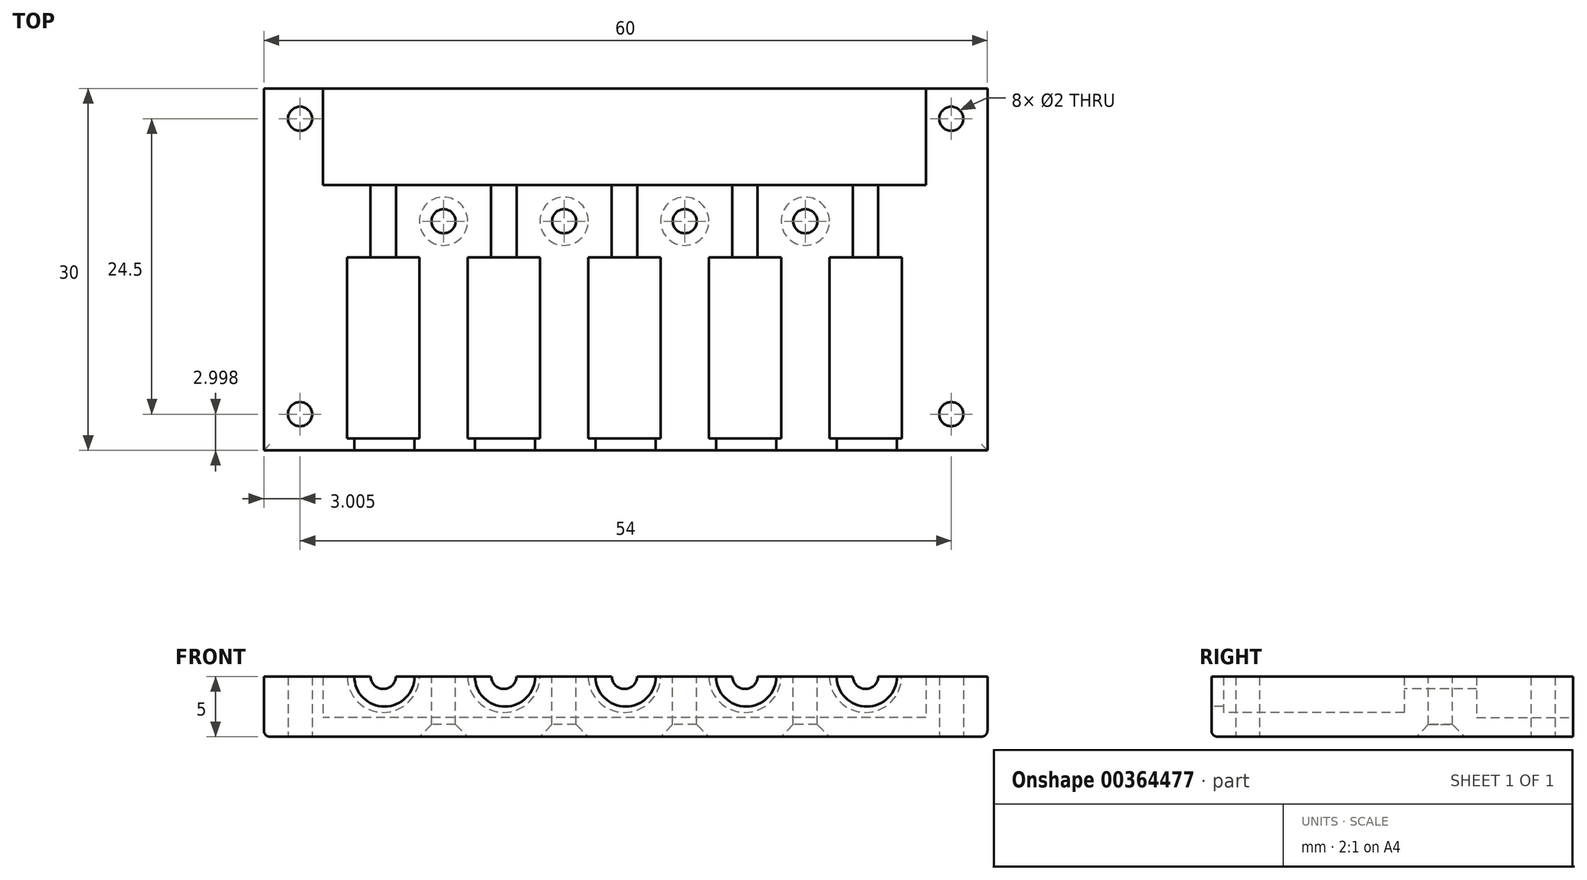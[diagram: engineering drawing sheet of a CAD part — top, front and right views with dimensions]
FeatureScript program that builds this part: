
annotation { "Feature Type Name" : "Feature", "Feature Type Description" : "" }
export const myFeature = defineFeature(function(context is Context, id is Id, definition is map)
    precondition{}
    {
        {
            var Q0;
            Q0=qCreatedBy(makeId("Top.planeOp"),FACE);
            var sketch = newSketch(context, id + "F0", { "sketchPlane" : qUnion([Q0])});
            skLineSegment(sketch, "E0.bottom", {"start": v(-32.95, 5.2) * mm, "end": v(27.05, 5.2) * mm});
            skLineSegment(sketch, "E0.top", {"start": v(-32.95, -19.8) * mm, "end": v(27.05, -19.8) * mm});
            skLineSegment(sketch, "E0.left", {"start": v(-32.95, 5.2) * mm, "end": v(-32.95, -19.8) * mm});
            skLineSegment(sketch, "E0.right", {"start": v(27.05, 5.2) * mm, "end": v(27.05, -19.8) * mm});
            skSolve(sketch);
        }
        {
            var Q0;
            Q0 = qSketchRegion(id + "F0", true);
            extrude(context, id + "F1", {"entities" : qUnion([Q0]), "depth" : 5 * mm});
        }
        {
            var Q0;
            Q0=makeQuery(id+"F1.opExtrude","SWEPT_FACE",FACE,{"disambiguationData":[OSD([sQuery(id+"F0.wireOp",EDGE,"E0.top")])]});
            var sketch = newSketch(context, id + "F2", { "sketchPlane" : qUnion([Q0])});
            skCircle(sketch, "E1", {"center": v(-22.95, 5) * mm, "radius": 2.5 * mm});
            skCircle(sketch, "E2.1.0.0", {"center": v(-12.95, 5) * mm, "radius": 2.5 * mm});
            skCircle(sketch, "E2.2.0.0", {"center": v(-2.95, 5) * mm, "radius": 2.5 * mm});
            skCircle(sketch, "E2.3.0.0", {"center": v(7.05, 5) * mm, "radius": 2.5 * mm});
            skCircle(sketch, "E2.4.0.0", {"center": v(17.05, 5) * mm, "radius": 2.5 * mm});
            skLineSegment(sketch, "E2.direction1", {"start": v(-22.95, 5) * mm, "end": v(-12.95, 5) * mm, "construction": true});
            skSolve(sketch);
        }
        {
            var Q0;
            Q0 = qSketchRegion(id + "F2", true);
            extrude(context, id + "F3", {"entities" : qUnion([Q0]), "operationType" : NewBodyOperationType.REMOVE, "oppositeDirection" : true, "depth" : 10 * mm});
        }
        {
            var Q0;
            Q0=makeQuery(id+"F1.opExtrude","SWEPT_FACE",FACE,{"disambiguationData":[OSD([sQuery(id+"F0.wireOp",EDGE,"E0.top")])]});
            cPlane(context, id + "F4", {"entities" : qUnion([Q0]), "cplaneType" : CPlaneType.OFFSET, "offset" : 1 * mm, "oppositeDirection" : true, "width" : 150 * mm, "height" : 150 * mm});
        }
        {
            var Q0;
            Q0=qCreatedBy(id+"F4.planeOp",FACE);
            var sketch = newSketch(context, id + "F5", { "sketchPlane" : qUnion([Q0])});
            skCircle(sketch, "E3", {"center": v(-23.05, 5.01) * mm, "radius": 3 * mm});
            skCircle(sketch, "E4.1.0.0", {"center": v(-13.05, 5.01) * mm, "radius": 3 * mm});
            skCircle(sketch, "E4.2.0.0", {"center": v(-3.05, 5.01) * mm, "radius": 3 * mm});
            skCircle(sketch, "E4.3.0.0", {"center": v(6.95, 5.01) * mm, "radius": 3 * mm});
            skCircle(sketch, "E4.4.0.0", {"center": v(16.95, 5.01) * mm, "radius": 3 * mm});
            skLineSegment(sketch, "E4.direction1", {"start": v(-23.05, 5.01) * mm, "end": v(-13.05, 5.01) * mm, "construction": true});
            skSolve(sketch);
        }
        {
            var Q0;
            Q0 = qSketchRegion(id + "F5", true);
            extrude(context, id + "F6", {"entities" : qUnion([Q0]), "operationType" : NewBodyOperationType.REMOVE, "oppositeDirection" : true, "depth" : 15 * mm});
        }
        {
            var Q0;
            Q0=makeQuery(id+"F6.boolean.opBoolean","COPY",FACE,{"derivedFrom":makeQuery(id+"F6.opExtrude","CAP_FACE",FACE,{"disambiguationData":[OSD([sQuery(id+"F5.wireOp",EDGE,"E3")])],"isStart":false})});
            var sketch = newSketch(context, id + "F7", { "sketchPlane" : qUnion([Q0])});
            skCircle(sketch, "E5", {"center": v(-23.05, 5.01) * mm, "radius": 1.05 * mm});
            skCircle(sketch, "E6.1.0.0", {"center": v(-13.05, 5.01) * mm, "radius": 1.05 * mm});
            skCircle(sketch, "E6.2.0.0", {"center": v(-3.05, 5.01) * mm, "radius": 1.05 * mm});
            skCircle(sketch, "E6.3.0.0", {"center": v(6.95, 5.01) * mm, "radius": 1.05 * mm});
            skCircle(sketch, "E6.4.0.0", {"center": v(16.95, 5.01) * mm, "radius": 1.05 * mm});
            skLineSegment(sketch, "E6.direction1", {"start": v(-23.05, 5.01) * mm, "end": v(-13.05, 5.01) * mm, "construction": true});
            skSolve(sketch);
        }
        {
            var Q0;
            Q0 = qSketchRegion(id + "F7", true);
            extrude(context, id + "F8", {"entities" : qUnion([Q0]), "operationType" : NewBodyOperationType.REMOVE, "oppositeDirection" : true, "depth" : 29 * mm});
        }
        {
            var Q0;
            Q0=makeQuery(id+"F1.opExtrude","SWEPT_FACE",FACE,{"disambiguationData":[OSD([sQuery(id+"F0.wireOp",EDGE,"E0.bottom")])]});
            var sketch = newSketch(context, id + "F9", { "sketchPlane" : qUnion([Q0])});
            skLineSegment(sketch, "E7.bottom", {"start": v(-21.95, 5) * mm, "end": v(28.05, 5) * mm});
            skLineSegment(sketch, "E7.top", {"start": v(-21.95, 1.58) * mm, "end": v(28.05, 1.58) * mm});
            skLineSegment(sketch, "E7.left", {"start": v(-21.95, 5) * mm, "end": v(-21.95, 1.58) * mm});
            skLineSegment(sketch, "E7.right", {"start": v(28.05, 5) * mm, "end": v(28.05, 1.58) * mm});
            skSolve(sketch);
        }
        {
            var Q0;
            Q0 = qSketchRegion(id + "F9", true);
            extrude(context, id + "F10", {"entities" : qUnion([Q0]), "operationType" : NewBodyOperationType.REMOVE, "oppositeDirection" : true, "depth" : 3 * mm});
        }
        {
            var Q0;
            Q0=makeQuery(id+"F1.opExtrude","SWEPT_FACE",FACE,{"disambiguationData":[OSD([sQuery(id+"F0.wireOp",EDGE,"E0.bottom")])]});
            extrude(context, id + "F11", {"entities" : qUnion([Q0]), "operationType" : NewBodyOperationType.ADD, "depth" : 5 * mm});
        }
        {
            var Q0;
            {var subQ0=sQuery(id+"F0.wireOp",EDGE,"E0.right");var subQ1=sQuery(id+"F0.wireOp",EDGE,"E0.bottom");Q0=makeQuery(id+"F11.boolean.opBoolean","MERGE",EDGE,{"derivedFrom":[makeQuery(id+"F1.opExtrude","CAP_EDGE",EDGE,{"disambiguationData":[OSD([subQ0])],"isStart":true}),makeQuery(id+"F11.opExtrude","SWEPT_EDGE",EDGE,{"disambiguationData":[OSD([subQ1,subQ0]),TDD([makeQuery(id+"F1.opExtrude","CAP_VERTEX",VERTEX,{"disambiguationData":[OSD([subQ1,subQ0])],"isStart":true})])]})]});}
            var Q1;
            Q1=makeQuery(id+"F1.opExtrude","CAP_EDGE",EDGE,{"disambiguationData":[OSD([sQuery(id+"F0.wireOp",EDGE,"E0.top")])],"isStart":true});
            var Q2;
            Q2=makeQuery(id+"FEIolAkUxVgGt6m_1.opLoft","SWEPT_EDGE",EDGE,{"disambiguationData":[OSD([sQuery(id+"F0.wireOp",EDGE,"E0.bottom"),sQuery(id+"F0.wireOp",EDGE,"E0.right"),sQuery(id+"F4cxA0SiljIs9s8_1.wireOp",EDGE,"Jk4UEFDV-4BQ6-7r7a-iLyf-OHepFeUpgrdx.top"),sQuery(id+"F4cxA0SiljIs9s8_1.wireOp",EDGE,"Jk4UEFDV-4BQ6-7r7a-iLyf-OHepFeUpgrdx.left")])]});
            var Q3;
            Q3=makeQuery(id+"FEIolAkUxVgGt6m_1.opLoft","MID_CAP_EDGE",EDGE,{"disambiguationData":[OSD([sQuery(id+"F4cxA0SiljIs9s8_1.wireOp",EDGE,"Jk4UEFDV-4BQ6-7r7a-iLyf-OHepFeUpgrdx.top"),sQuery(id+"F4cxA0SiljIs9s8_1.wireOp",EDGE,"Jk4UEFDV-4BQ6-7r7a-iLyf-OHepFeUpgrdx.left"),sQuery(id+"F4cxA0SiljIs9s8_1.wireOp",EDGE,"Jk4UEFDV-4BQ6-7r7a-iLyf-OHepFeUpgrdx.right")])],"capPos":1.0});
            var Q4;
            Q4=makeQuery(id+"FEIolAkUxVgGt6m_1.opLoft","SWEPT_EDGE",EDGE,{"disambiguationData":[OSD([sQuery(id+"F0.wireOp",EDGE,"E0.bottom"),sQuery(id+"F0.wireOp",EDGE,"E0.left"),sQuery(id+"F4cxA0SiljIs9s8_1.wireOp",EDGE,"Jk4UEFDV-4BQ6-7r7a-iLyf-OHepFeUpgrdx.top"),sQuery(id+"F4cxA0SiljIs9s8_1.wireOp",EDGE,"Jk4UEFDV-4BQ6-7r7a-iLyf-OHepFeUpgrdx.right")])]});
            var Q5;
            {var subQ0=sQuery(id+"F0.wireOp",EDGE,"E0.left");var subQ1=sQuery(id+"F0.wireOp",EDGE,"E0.bottom");Q5=makeQuery(id+"F11.boolean.opBoolean","MERGE",EDGE,{"derivedFrom":[makeQuery(id+"F1.opExtrude","CAP_EDGE",EDGE,{"disambiguationData":[OSD([subQ0])],"isStart":true}),makeQuery(id+"F11.opExtrude","SWEPT_EDGE",EDGE,{"disambiguationData":[OSD([subQ1,subQ0]),TDD([makeQuery(id+"F1.opExtrude","CAP_VERTEX",VERTEX,{"disambiguationData":[OSD([subQ1,subQ0])],"isStart":true})])]})]});}
            fillet(context, id + "F12", {"entities" : qUnion([Q0, Q1, Q2, Q3, Q4, Q5]), "radius" : 0.5 * mm, "tangentPropagation" : true, "allowEdgeOverflow" : false});
        }
        {
            var Q0;
            {var subQ0=sQuery(id+"F0.wireOp",EDGE,"E0.bottom");Q0=makeQuery(id+"F11.boolean.opBoolean","MERGE",FACE,{"derivedFrom":[makeQuery(id+"F1.opExtrude","CAP_FACE",FACE,{"disambiguationData":[OSD([subQ0,sQuery(id+"F0.wireOp",EDGE,"E0.top"),sQuery(id+"F0.wireOp",EDGE,"E0.left"),sQuery(id+"F0.wireOp",EDGE,"E0.right")])],"isStart":true}),makeQuery(id+"F11.opExtrude","SWEPT_FACE",FACE,{"disambiguationData":[OSD([subQ0]),TDD([makeQuery(id+"F1.opExtrude","CAP_EDGE",EDGE,{"disambiguationData":[OSD([subQ0])],"isStart":true})])]})]});}
            var sketch = newSketch(context, id + "F13", { "sketchPlane" : qUnion([Q0])});
            skLineSegment(sketch, "E8", {"start": v(-2.95, 19.3) * mm, "end": v(-2.95, -10.2) * mm});
            skCircle(sketch, "E9", {"center": v(-29.95, 16.8) * mm, "radius": 1 * mm});
            skCircle(sketch, "E10.MirrorC", {"center": v(24.05, 16.8) * mm, "radius": 1 * mm});
            skSolve(sketch);
        }
        {
            var Q0;
            {var subQ7=sQuery(id+"F13.wireOp",EDGE,"E8");Q0=makeQuery(id+"F13.imprint","IMPRINT",FACE,{"disambiguationData":[TD([[makeQuery(id+"F13.imprint","IMPRINT",EDGE,{"derivedFrom":subQ7}),-1.0]])]});}
            var sketch = newSketch(context, id + "F14", { "sketchPlane" : qUnion([Q0])});
            skCircle(sketch, "E11", {"center": v(-29.95, -7.7) * mm, "radius": 1 * mm});
            skCircle(sketch, "E12.MirrorC", {"center": v(24.05, -7.7) * mm, "radius": 1 * mm});
            skSolve(sketch);
        }
        {
            var Q0;
            Q0 = qSketchRegion(id + "F14", true);
            var Q1;
            Q1 = qSketchRegion(id + "F13", true);
            extrude(context, id + "F15", {"entities" : qUnion([Q0, Q1]), "operationType" : NewBodyOperationType.REMOVE, "endBound" : BoundingType.THROUGH_ALL, "oppositeDirection" : true, "depth" : 25 * mm});
        }
        {
            var Q0;
            {var subQ0=sQuery(id+"F5.wireOp",EDGE,"E4.4.0.0");var subQ1=sQuery(id+"F0.wireOp",EDGE,"E0.top");var subQ2=sQuery(id+"F5.wireOp",EDGE,"E4.3.0.0");var subQ3=sQuery(id+"F0.wireOp",EDGE,"E0.bottom");Q0=makeQuery(id+"F8.boolean.opBoolean","SPLIT",FACE,{"disambiguationData":[TD([makeQuery(id+"F1.opExtrude","SWEPT_FACE",FACE,{"disambiguationData":[OSD([subQ3])]}),makeQuery(id+"F1.opExtrude","SWEPT_FACE",FACE,{"disambiguationData":[OSD([subQ1])]}),makeQuery(id+"F3.boolean.opBoolean","COPY",FACE,{"derivedFrom":makeQuery(id+"F3.opExtrude","SWEPT_FACE",FACE,{"disambiguationData":[OSD([sQuery(id+"F2.wireOp",EDGE,"E2.3.0.0")])]})}),makeQuery(id+"F3.boolean.opBoolean","COPY",FACE,{"derivedFrom":makeQuery(id+"F3.opExtrude","SWEPT_FACE",FACE,{"disambiguationData":[OSD([sQuery(id+"F2.wireOp",EDGE,"E2.4.0.0")])]})}),makeQuery(id+"F6.boolean.opBoolean","COPY",FACE,{"derivedFrom":makeQuery(id+"F6.opExtrude","SWEPT_FACE",FACE,{"disambiguationData":[OSD([subQ2])]})}),makeQuery(id+"F6.boolean.opBoolean","COPY",FACE,{"derivedFrom":makeQuery(id+"F6.opExtrude","CAP_FACE",FACE,{"disambiguationData":[OSD([subQ2])],"isStart":true})}),makeQuery(id+"F6.boolean.opBoolean","COPY",FACE,{"derivedFrom":makeQuery(id+"F6.opExtrude","CAP_FACE",FACE,{"disambiguationData":[OSD([subQ2])],"isStart":false})}),makeQuery(id+"F6.boolean.opBoolean","COPY",FACE,{"derivedFrom":makeQuery(id+"F6.opExtrude","SWEPT_FACE",FACE,{"disambiguationData":[OSD([subQ0])]})}),makeQuery(id+"F6.boolean.opBoolean","COPY",FACE,{"derivedFrom":makeQuery(id+"F6.opExtrude","CAP_FACE",FACE,{"disambiguationData":[OSD([subQ0])],"isStart":true})}),makeQuery(id+"F6.boolean.opBoolean","COPY",FACE,{"derivedFrom":makeQuery(id+"F6.opExtrude","CAP_FACE",FACE,{"disambiguationData":[OSD([subQ0])],"isStart":false})}),makeQuery(id+"F8.opExtrude","SWEPT_FACE",FACE,{"disambiguationData":[OSD([sQuery(id+"F7.wireOp",EDGE,"E6.3.0.0")])]}),makeQuery(id+"F8.opExtrude","SWEPT_FACE",FACE,{"disambiguationData":[OSD([sQuery(id+"F7.wireOp",EDGE,"E6.4.0.0")])]})])],"derivedFrom":makeQuery(id+"F1.opExtrude","CAP_FACE",FACE,{"disambiguationData":[OSD([subQ3,subQ1,sQuery(id+"F0.wireOp",EDGE,"E0.left"),sQuery(id+"F0.wireOp",EDGE,"E0.right")])],"isStart":false})});}
            var sketch = newSketch(context, id + "F16", { "sketchPlane" : qUnion([Q0])});
            skCircle(sketch, "E13", {"center": v(11.95, -0.8) * mm, "radius": 1 * mm});
            skCircle(sketch, "E14.1.0.0", {"center": v(1.95, -0.8) * mm, "radius": 1 * mm});
            skCircle(sketch, "E14.2.0.0", {"center": v(-8.05, -0.8) * mm, "radius": 1 * mm});
            skCircle(sketch, "E14.3.0.0", {"center": v(-18.05, -0.8) * mm, "radius": 1 * mm});
            skLineSegment(sketch, "E14.direction1", {"start": v(11.95, -0.8) * mm, "end": v(1.95, -0.8) * mm, "construction": true});
            skSolve(sketch);
        }
        {
            var Q0;
            Q0 = qSketchRegion(id + "F16", true);
            extrude(context, id + "F17", {"entities" : qUnion([Q0]), "operationType" : NewBodyOperationType.REMOVE, "endBound" : BoundingType.THROUGH_ALL, "oppositeDirection" : true, "depth" : 25 * mm});
        }
        {
            var Q0;
            Q0=makeQuery(id+"F15.boolean.opBoolean","COPY",EDGE,{"derivedFrom":makeQuery(id+"F15.opExtrude","CAP_EDGE",EDGE,{"disambiguationData":[OSD([sQuery(id+"F14.wireOp",EDGE,"E12.MirrorC")])],"isStart":true})});
            var Q1;
            {var subQ0=sQuery(id+"F0.wireOp",EDGE,"E0.bottom");Q1=makeQuery(id+"F17.boolean.opBoolean","INTERSECT",EDGE,{"derivedFrom":[makeQuery(id+"F11.boolean.opBoolean","MERGE",FACE,{"derivedFrom":[makeQuery(id+"F1.opExtrude","CAP_FACE",FACE,{"disambiguationData":[OSD([subQ0,sQuery(id+"F0.wireOp",EDGE,"E0.top"),sQuery(id+"F0.wireOp",EDGE,"E0.left"),sQuery(id+"F0.wireOp",EDGE,"E0.right")])],"isStart":true}),makeQuery(id+"F11.opExtrude","SWEPT_FACE",FACE,{"disambiguationData":[OSD([subQ0]),TDD([makeQuery(id+"F1.opExtrude","CAP_EDGE",EDGE,{"disambiguationData":[OSD([subQ0])],"isStart":true})])]})]}),makeQuery(id+"F17.opExtrude","SWEPT_FACE",FACE,{"disambiguationData":[OSD([sQuery(id+"F16.wireOp",EDGE,"E13")])]})]});}
            var Q2;
            Q2=makeQuery(id+"F15.boolean.opBoolean","COPY",EDGE,{"derivedFrom":makeQuery(id+"F15.opExtrude","CAP_EDGE",EDGE,{"disambiguationData":[OSD([sQuery(id+"F13.wireOp",EDGE,"E10.MirrorC")])],"isStart":true})});
            var Q3;
            {var subQ0=sQuery(id+"F0.wireOp",EDGE,"E0.bottom");Q3=makeQuery(id+"F17.boolean.opBoolean","INTERSECT",EDGE,{"derivedFrom":[makeQuery(id+"F11.boolean.opBoolean","MERGE",FACE,{"derivedFrom":[makeQuery(id+"F1.opExtrude","CAP_FACE",FACE,{"disambiguationData":[OSD([subQ0,sQuery(id+"F0.wireOp",EDGE,"E0.top"),sQuery(id+"F0.wireOp",EDGE,"E0.left"),sQuery(id+"F0.wireOp",EDGE,"E0.right")])],"isStart":true}),makeQuery(id+"F11.opExtrude","SWEPT_FACE",FACE,{"disambiguationData":[OSD([subQ0]),TDD([makeQuery(id+"F1.opExtrude","CAP_EDGE",EDGE,{"disambiguationData":[OSD([subQ0])],"isStart":true})])]})]}),makeQuery(id+"F17.opExtrude","SWEPT_FACE",FACE,{"disambiguationData":[OSD([sQuery(id+"F16.wireOp",EDGE,"E14.1.0.0")])]})]});}
            var Q4;
            {var subQ0=sQuery(id+"F0.wireOp",EDGE,"E0.bottom");Q4=makeQuery(id+"F17.boolean.opBoolean","INTERSECT",EDGE,{"derivedFrom":[makeQuery(id+"F11.boolean.opBoolean","MERGE",FACE,{"derivedFrom":[makeQuery(id+"F1.opExtrude","CAP_FACE",FACE,{"disambiguationData":[OSD([subQ0,sQuery(id+"F0.wireOp",EDGE,"E0.top"),sQuery(id+"F0.wireOp",EDGE,"E0.left"),sQuery(id+"F0.wireOp",EDGE,"E0.right")])],"isStart":true}),makeQuery(id+"F11.opExtrude","SWEPT_FACE",FACE,{"disambiguationData":[OSD([subQ0]),TDD([makeQuery(id+"F1.opExtrude","CAP_EDGE",EDGE,{"disambiguationData":[OSD([subQ0])],"isStart":true})])]})]}),makeQuery(id+"F17.opExtrude","SWEPT_FACE",FACE,{"disambiguationData":[OSD([sQuery(id+"F16.wireOp",EDGE,"E14.2.0.0")])]})]});}
            var Q5;
            {var subQ0=sQuery(id+"F0.wireOp",EDGE,"E0.bottom");Q5=makeQuery(id+"F17.boolean.opBoolean","INTERSECT",EDGE,{"derivedFrom":[makeQuery(id+"F11.boolean.opBoolean","MERGE",FACE,{"derivedFrom":[makeQuery(id+"F1.opExtrude","CAP_FACE",FACE,{"disambiguationData":[OSD([subQ0,sQuery(id+"F0.wireOp",EDGE,"E0.top"),sQuery(id+"F0.wireOp",EDGE,"E0.left"),sQuery(id+"F0.wireOp",EDGE,"E0.right")])],"isStart":true}),makeQuery(id+"F11.opExtrude","SWEPT_FACE",FACE,{"disambiguationData":[OSD([subQ0]),TDD([makeQuery(id+"F1.opExtrude","CAP_EDGE",EDGE,{"disambiguationData":[OSD([subQ0])],"isStart":true})])]})]}),makeQuery(id+"F17.opExtrude","SWEPT_FACE",FACE,{"disambiguationData":[OSD([sQuery(id+"F16.wireOp",EDGE,"E14.3.0.0")])]})]});}
            var Q6;
            Q6=makeQuery(id+"F15.boolean.opBoolean","COPY",EDGE,{"derivedFrom":makeQuery(id+"F15.opExtrude","CAP_EDGE",EDGE,{"disambiguationData":[OSD([sQuery(id+"F14.wireOp",EDGE,"E11")])],"isStart":true})});
            var Q7;
            Q7=makeQuery(id+"F15.boolean.opBoolean","COPY",EDGE,{"derivedFrom":makeQuery(id+"F15.opExtrude","CAP_EDGE",EDGE,{"disambiguationData":[OSD([sQuery(id+"F13.wireOp",EDGE,"E9")])],"isStart":true})});
            chamfer(context, id + "F18", {"entities" : qUnion([Q0, Q1, Q2, Q3, Q4, Q5, Q6, Q7]), "width" : 1 * mm, "tangentPropagation" : true});
        }
    });
